# Revit family: Faucet-Kitchen-Grohe-Concetto-3134910E
name_source: partatom
category: Plumbing Fixtures
units: mm (PartAtom-declared; Revit-internal decimal feet)

## family parameters
Always vertical = No
Cut with Voids When Loaded = No
OmniClass Number = 23.45.55.14
OmniClass Title = Single Faucets
Part Type = Normal
Room Calculation Point = No
Round Connector Dimension = Use Diameter
Shared = Yes
Work Plane-Based = Yes

## types (3) — shared parameters
ADA Compliant = Yes
Assembly Code = D2020300
CW Connection = Yes
CWFU = 1.5
CalGreen Compliant = Yes
Cold Water Connection Diameter = 3/8"
Default Elevation = 0"
Flow Rate = 1.5 gpm (5.7 L/min)
HW Connection = Yes
HWFU = 1.5
Height = 15"
Hot Water Connection Diameter = 0"
Installation Type = Deck Mounted
Length = 8 9/16"
Manufacturer = Grohe
Price = Prices may vary. Please consult Manufacturer Representative for most up-to-date price list.
Product Documentation Link = https://americanstandard.box.com
Product Page URL = https://www.grohe.us
Revised Date = 3/29/2021
URL = http://www.grohe.com
Vent Connection = No
WFU = 2
Warranty Documentation Link = https://cdn.cloud.grohe.com
Waste Connection = No
Width = 2"
cUPC Compliant = Yes

## per-type parameters (varying)
| type | Description | Finish | Material |
| 3134910E | CONCETTO Single-Handle Kitchen Faucet Starlight Chrome | Metal-Grohe-003-Starlight Chrome | Metal-Grohe-003-Starlight Chrome |
| 31349DCE | CONCETTO Single-Handle Kitchen Faucet SuperSteel Infinity Finish | Metal-Grohe-DCE-SuperSteel Infinity Finish | Metal-Grohe-DCE-SuperSteel Infinity Finish |
| 3134900E | CONCETTO Single-Handle Kitchen Faucet Starlight Chrome | Metal-Grohe-003-Starlight Chrome | Metal-Grohe-003-Starlight Chrome |

note: column(s) folded — value = type name in every type: Model

## geometry (parser evidence)
native form markers: Sweep x2
no freeform markers — native parametric forms only
